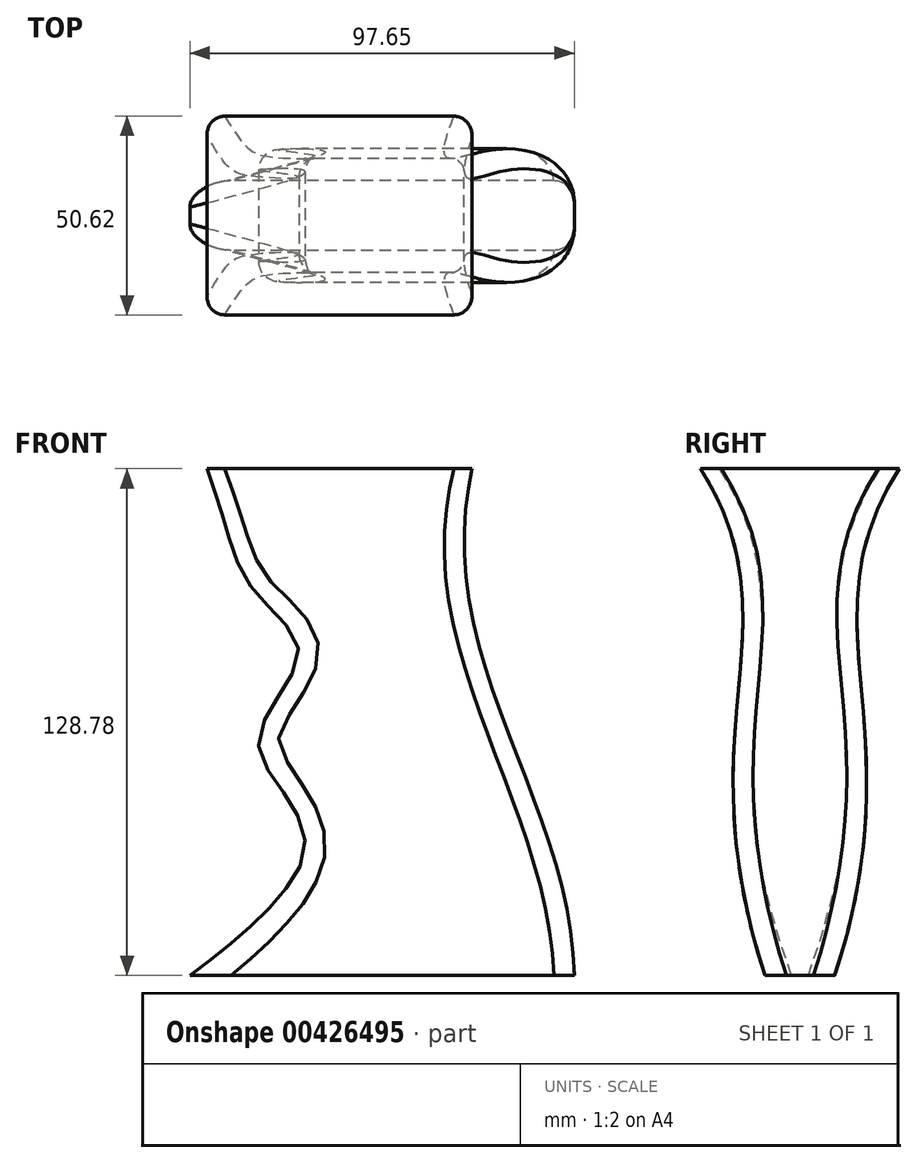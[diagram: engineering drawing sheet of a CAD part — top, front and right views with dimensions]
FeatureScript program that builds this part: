
annotation { "Feature Type Name" : "Feature", "Feature Type Description" : "" }
export const myFeature = defineFeature(function(context is Context, id is Id, definition is map)
    precondition{}
    {
        {
            var Q0;
            Q0=qCreatedBy(makeId("Top.planeOp"),FACE);
            var sketch = newSketch(context, id + "F0", { "sketchPlane" : qUnion([Q0])});
            skLineSegment(sketch, "E0.bottom", {"start": v(-58.83, 0) * mm, "end": v(41.48, 0) * mm});
            skLineSegment(sketch, "E0.top", {"start": v(-58.83, -30.07) * mm, "end": v(41.48, -30.07) * mm});
            skLineSegment(sketch, "E0.left", {"start": v(-58.83, 0) * mm, "end": v(-58.83, -30.07) * mm});
            skLineSegment(sketch, "E0.right", {"start": v(41.48, 0) * mm, "end": v(41.48, -30.07) * mm});
            skSolve(sketch);
        }
        {
            var Q0;
            Q0 = qSketchRegion(id + "F0", true);
            extrude(context, id + "F1", {"entities" : qUnion([Q0]), "depth" : 128.78 * mm, "offsetDistance" : 25.4 * mm});
        }
        {
            var Q0;
            Q0=makeQuery(id+"F1.opExtrude","SWEPT_FACE",FACE,{"disambiguationData":[OSD([sQuery(id+"F0.wireOp",EDGE,"E0.left")])]});
            var sketch = newSketch(context, id + "F2", { "sketchPlane" : qUnion([Q0])});
            skLineSegment(sketch, "E1.bottom", {"start": v(0, 128.78) * mm, "end": v(50.44, 128.78) * mm});
            skLineSegment(sketch, "E1.top", {"start": v(0, 0) * mm, "end": v(50.44, 0) * mm});
            skLineSegment(sketch, "E1.left", {"start": v(0, 128.78) * mm, "end": v(0, 0) * mm});
            skLineSegment(sketch, "E1.right", {"start": v(50.44, 128.78) * mm, "end": v(50.44, 0) * mm});
            skFitSpline(sketch, "E2", {"points": [v(25.22, 128.78) * mm, v(8.83, 0) * mm], "startDerivative": vector(-75.67, -120.24) * mm, "endDerivative": vector(-63.7, -193.17) * mm});
            skPoint(sketch, "E3", {"position": v(15.03, 0) * mm});
            skSolve(sketch);
        }
        {
            var Q0;
            {var subQ2=sQuery(id+"F2.wireOp",EDGE,"E2");Q0=makeQuery(id+"F2.imprint","IMPRINT",FACE,{"disambiguationData":[TD([[makeQuery(id+"F2.imprint","IMPRINT",EDGE,{"derivedFrom":subQ2}),1.0]])]});}
            extrude(context, id + "F3", {"entities" : qUnion([Q0]), "operationType" : NewBodyOperationType.REMOVE, "oppositeDirection" : true, "depth" : 159 * mm, "offsetDistance" : 25.4 * mm});
        }
        {
            var Q0;
            Q0=makeQuery(id+"F1.opExtrude","SWEPT_FACE",FACE,{"disambiguationData":[OSD([sQuery(id+"F0.wireOp",EDGE,"E0.bottom")])]});
            var sketch = newSketch(context, id + "F4", { "sketchPlane" : qUnion([Q0])});
            skLineSegment(sketch, "E4.bottom", {"start": v(-45.71, 132.12) * mm, "end": v(81.58, 132.12) * mm});
            skLineSegment(sketch, "E4.top", {"start": v(-45.71, -5.4) * mm, "end": v(81.58, -5.4) * mm});
            skLineSegment(sketch, "E4.left", {"start": v(-45.71, 132.12) * mm, "end": v(-45.71, -5.4) * mm});
            skLineSegment(sketch, "E4.right", {"start": v(81.58, 132.12) * mm, "end": v(81.58, -5.4) * mm});
            skFitSpline(sketch, "E5", {"points": [v(-14.47, 132.12) * mm, v(-39.58, -5.4) * mm], "startDerivative": vector(41.17, -157.66) * mm, "endDerivative": vector(5.7, -148.9) * mm});
            skFitSpline(sketch, "E6", {"points": [v(55.01, 132.12) * mm, v(42.33, 98.55) * mm, v(30.36, 81.61) * mm, v(40.58, 58.55) * mm, v(29.2, 30.23) * mm, v(64.94, -5.4) * mm, v(64.65, -5.4) * mm], "startDerivative": vector(-91.73, -222.26) * mm, "endDerivative": vector(-7.01, 3.16) * mm});
            skSolve(sketch);
        }
        {
            var Q0;
            {var subQ1=sQuery(id+"F0.wireOp",EDGE,"E0.bottom");var subQ6=makeQuery(id+"F1.opExtrude","SWEPT_EDGE",EDGE,{"disambiguationData":[OSD([subQ1,sQuery(id+"F0.wireOp",EDGE,"E0.right")])]});Q0=makeQuery(id+"F4.imprint","IMPRINT",FACE,{"disambiguationData":[TD([[makeQuery(id+"F4.imprint","IMPRINT",EDGE,{"derivedFrom":subQ6}),1.0]])]});}
            var Q1;
            {var subQ1=sQuery(id+"F0.wireOp",EDGE,"E0.bottom");var subQ6=makeQuery(id+"F1.opExtrude","SWEPT_EDGE",EDGE,{"disambiguationData":[OSD([subQ1,sQuery(id+"F0.wireOp",EDGE,"E0.left")])]});Q1=makeQuery(id+"F4.imprint","IMPRINT",FACE,{"disambiguationData":[TD([[makeQuery(id+"F4.imprint","IMPRINT",EDGE,{"derivedFrom":subQ6}),-1.0]])]});}
            extrude(context, id + "F5", {"entities" : qUnion([Q0, Q1]), "operationType" : NewBodyOperationType.REMOVE, "oppositeDirection" : true, "depth" : 139.2 * mm, "offsetDistance" : 25.4 * mm});
        }
        {
            var Q0;
            Q0=makeQuery(id+"F5.boolean.opBoolean","INTERSECT",EDGE,{"derivedFrom":[makeQuery(id+"F3.boolean.opBoolean","COPY",FACE,{"derivedFrom":makeQuery(id+"F3.opExtrude","SWEPT_FACE",FACE,{"disambiguationData":[OSD([sQuery(id+"F2.wireOp",EDGE,"E2")])]})}),makeQuery(id+"F5.opExtrude","SWEPT_FACE",FACE,{"disambiguationData":[OSD([sQuery(id+"F4.wireOp",EDGE,"E5")])]})]});
            var Q1;
            {var subQ0=sQuery(id+"F0.wireOp",EDGE,"E0.top");Q1=makeQuery(id+"F3.boolean.opBoolean","MERGE",EDGE,{"derivedFrom":[makeQuery(id+"F1.opExtrude","CAP_EDGE",EDGE,{"disambiguationData":[OSD([subQ0])],"isStart":true}),makeQuery(id+"F3.opExtrude","SWEPT_EDGE",EDGE,{"disambiguationData":[OSD([subQ0,sQuery(id+"F0.wireOp",EDGE,"E0.left"),sQuery(id+"F2.wireOp",EDGE,"E1.top"),sQuery(id+"F2.wireOp",EDGE,"E2")])]})]});}
            fillet(context, id + "F6", {"entities" : qUnion([Q0, Q1]), "radius" : 5.08 * mm, "tangentPropagation" : true, "allowEdgeOverflow" : false});
        }
        {
            var Q0;
            Q0=makeQuery(id+"F5.boolean.opBoolean","INTERSECT",EDGE,{"derivedFrom":[makeQuery(id+"F3.boolean.opBoolean","COPY",FACE,{"derivedFrom":makeQuery(id+"F3.opExtrude","SWEPT_FACE",FACE,{"disambiguationData":[OSD([sQuery(id+"F2.wireOp",EDGE,"E2")])]})}),makeQuery(id+"F5.opExtrude","SWEPT_FACE",FACE,{"disambiguationData":[OSD([sQuery(id+"F4.wireOp",EDGE,"E6")])]})]});
            var Q1;
            Q1=makeQuery(id+"F3.boolean.opBoolean","COPY",EDGE,{"derivedFrom":makeQuery(id+"F3.opExtrude","SWEPT_EDGE",EDGE,{"disambiguationData":[OSD([sQuery(id+"F2.wireOp",EDGE,"E1.bottom"),sQuery(id+"F2.wireOp",EDGE,"E2")])]})});
            fillet(context, id + "F7", {"entities" : qUnion([Q0, Q1]), "radius" : 5.08 * mm, "tangentPropagation" : true, "allowEdgeOverflow" : false});
        }
        {
            var Q0;
            Q0=makeQuery(id+"F1.opExtrude","SWEPT_BODY",BODY,{"disambiguationData":[OSD([sQuery(id+"F0.wireOp",EDGE,"E0.bottom"),sQuery(id+"F0.wireOp",EDGE,"E0.top"),sQuery(id+"F0.wireOp",EDGE,"E0.left"),sQuery(id+"F0.wireOp",EDGE,"E0.right")])]});
            var Q1;
            Q1=makeQuery(id+"F1.opExtrude","SWEPT_FACE",FACE,{"disambiguationData":[OSD([sQuery(id+"F0.wireOp",EDGE,"E0.bottom")])]});
            mirror(context, id + "F8", {"operationType" : NewBodyOperationType.ADD, "entities" : qUnion([Q0]), "mirrorPlane" : qUnion([Q1])});
        }
    });
